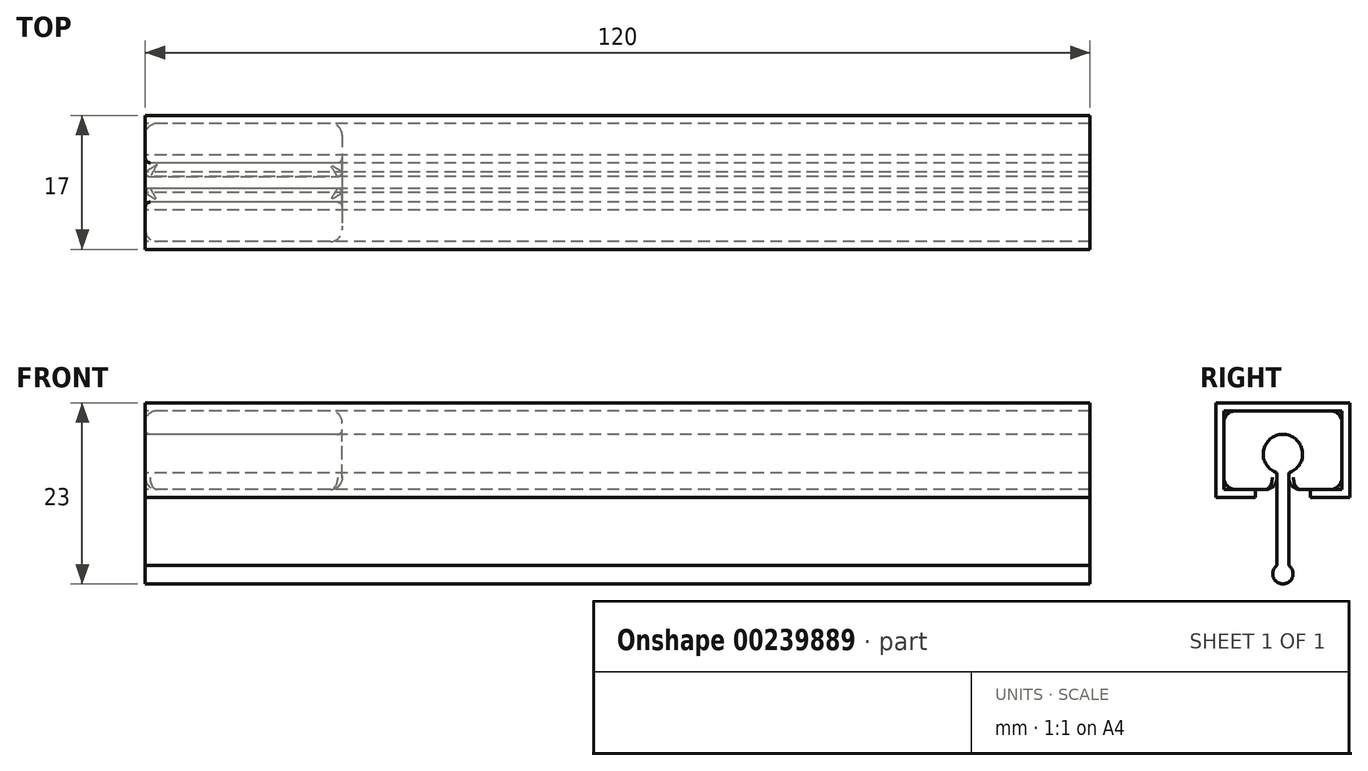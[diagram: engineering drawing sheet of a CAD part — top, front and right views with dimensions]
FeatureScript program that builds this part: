
annotation { "Feature Type Name" : "Feature", "Feature Type Description" : "" }
export const myFeature = defineFeature(function(context is Context, id is Id, definition is map)
    precondition{}
    {
        {
            var Q0;
            Q0=qCreatedBy(makeId("Right.planeOp"),FACE);
            var sketch = newSketch(context, id + "F0", { "sketchPlane" : qUnion([Q0])});
            skArc(sketch, "E0", {"start": v(0.75, -2.88) * mm, "mid": v(0, 2) * mm, "end": v(-0.75, -2.88) * mm});
            skArc(sketch, "E1", {"start": v(-0.75, -14.64) * mm, "mid": v(0, -17) * mm, "end": v(0.75, -14.64) * mm});
            skLineSegment(sketch, "E2", {"start": v(0.75, -2.88) * mm, "end": v(0.75, -14.64) * mm});
            skLineSegment(sketch, "E3", {"start": v(-0.75, -14.64) * mm, "end": v(-0.75, -2.88) * mm});
            skLineSegment(sketch, "E4.bottom", {"start": v(7.5, -5) * mm, "end": v(-7.5, -5) * mm});
            skLineSegment(sketch, "E4.top", {"start": v(7.5, 5) * mm, "end": v(-7.5, 5) * mm});
            skLineSegment(sketch, "E4.left", {"start": v(7.5, -5) * mm, "end": v(7.5, 5) * mm});
            skLineSegment(sketch, "E4.right", {"start": v(-7.5, -5) * mm, "end": v(-7.5, 5) * mm});
            skPoint(sketch, "E4.middle", {"position": v(0, 0) * mm});
            skSolve(sketch);
        }
        {
            var Q0;
            {var subQ5=sQuery(id+"F0.wireOp",EDGE,"E0");Q0=makeQuery(id+"F0.imprint","IMPRINT",FACE,{"disambiguationData":[TD([[makeQuery(id+"F0.imprint","IMPRINT",EDGE,{"derivedFrom":subQ5}),-1.0]])]});}
            extrude(context, id + "F1", {"entities" : qUnion([Q0]), "depth" : 25 * mm});
        }
        {
            var Q0;
            Q0=makeQuery(id+"F1.opExtrude","SWEPT_FACE",FACE,{"disambiguationData":[OSD([sQuery(id+"F0.wireOp",EDGE,"E4.left")])]});
            var Q1;
            Q1=makeQuery(id+"F1.opExtrude","SWEPT_FACE",FACE,{"disambiguationData":[OSD([sQuery(id+"F0.wireOp",EDGE,"E4.top")])]});
            var Q2;
            Q2=makeQuery(id+"F1.opExtrude","SWEPT_FACE",FACE,{"disambiguationData":[OSD([sQuery(id+"F0.wireOp",EDGE,"E4.right")])]});
            var Q3;
            {var subQ0=sQuery(id+"F0.wireOp",EDGE,"E4.bottom");Q3=makeQuery(id+"F1.opExtrude","SWEPT_FACE",FACE,{"disambiguationData":[OSD([subQ0]),TDD([makeQuery(id+"F0.imprint","IMPRINT",EDGE,{"disambiguationData":[TD([[makeQuery(id+"F0.imprint","INTERSECT",VERTEX,{"derivedFrom":[subQ0,sQuery(id+"F0.wireOp",EDGE,"E4.right")]}),1.0]])],"derivedFrom":subQ0})])]});}
            var Q4;
            {var subQ0=sQuery(id+"F0.wireOp",EDGE,"E4.bottom");Q4=makeQuery(id+"F1.opExtrude","SWEPT_FACE",FACE,{"disambiguationData":[OSD([subQ0]),TDD([makeQuery(id+"F0.imprint","IMPRINT",EDGE,{"disambiguationData":[TD([[makeQuery(id+"F0.imprint","INTERSECT",VERTEX,{"derivedFrom":[subQ0,sQuery(id+"F0.wireOp",EDGE,"E4.left")]}),-1.0]])],"derivedFrom":subQ0})])]});}
            var Q5;
            {var subQ0=sQuery(id+"F0.wireOp",EDGE,"E4.bottom");Q5=makeQuery(id+"F1.opExtrude","CAP_EDGE",EDGE,{"disambiguationData":[OSD([subQ0]),TDD([makeQuery(id+"F0.imprint","IMPRINT",EDGE,{"disambiguationData":[TD([[makeQuery(id+"F0.imprint","INTERSECT",VERTEX,{"derivedFrom":[subQ0,sQuery(id+"F0.wireOp",EDGE,"E4.left")]}),-1.0]])],"derivedFrom":subQ0})])],"isStart":false});}
            var Q6;
            Q6=makeQuery(id+"F1.opExtrude","SWEPT_EDGE",EDGE,{"disambiguationData":[OSD([sQuery(id+"F0.wireOp",EDGE,"E4.bottom"),sQuery(id+"F0.wireOp",EDGE,"E4.left")])]});
            var Q7;
            Q7=makeQuery(id+"F1.opExtrude","SWEPT_EDGE",EDGE,{"disambiguationData":[OSD([sQuery(id+"F0.wireOp",EDGE,"E4.bottom"),sQuery(id+"F0.wireOp",EDGE,"E4.right")])]});
            fillet(context, id + "F2", {"entities" : qUnion([Q0, Q1, Q2, Q3, Q4, Q5, Q6, Q7]), "radius" : 1.5 * mm, "tangentPropagation" : true, "allowEdgeOverflow" : false});
        }
        {
            var Q0;
            Q0=makeQuery(id+"F1.opExtrude","SWEPT_FACE",FACE,{"disambiguationData":[OSD([sQuery(id+"F0.wireOp",EDGE,"E0")])]});
            var Q1;
            Q1=makeQuery(id+"F1.opExtrude","CAP_EDGE",EDGE,{"disambiguationData":[OSD([sQuery(id+"F0.wireOp",EDGE,"E3")])],"isStart":false});
            var Q2;
            Q2=makeQuery(id+"F1.opExtrude","CAP_EDGE",EDGE,{"disambiguationData":[OSD([sQuery(id+"F0.wireOp",EDGE,"E2")])],"isStart":false});
            var Q3;
            Q3=makeQuery(id+"F1.opExtrude","CAP_EDGE",EDGE,{"disambiguationData":[OSD([sQuery(id+"F0.wireOp",EDGE,"E3")])],"isStart":true});
            var Q4;
            Q4=makeQuery(id+"F1.opExtrude","CAP_EDGE",EDGE,{"disambiguationData":[OSD([sQuery(id+"F0.wireOp",EDGE,"E2")])],"isStart":true});
            fillet(context, id + "F3", {"entities" : qUnion([Q0, Q1, Q2, Q3, Q4]), "radius" : .6 * mm, "tangentPropagation" : true, "allowEdgeOverflow" : false});
        }
        {
            var Q0;
            {var subQ0=sQuery(id+"F0.wireOp",EDGE,"E0");Q0=makeQuery(id+"F0.imprint","IMPRINT",FACE,{"disambiguationData":[TD([[makeQuery(id+"F0.imprint","IMPRINT",EDGE,{"derivedFrom":subQ0}),1.0]])]});}
            var Q1;
            {var subQ0=sQuery(id+"F0.wireOp",EDGE,"E1");Q1=makeQuery(id+"F0.imprint","IMPRINT",FACE,{"disambiguationData":[TD([[makeQuery(id+"F0.imprint","IMPRINT",EDGE,{"derivedFrom":subQ0}),1.0]])]});}
            extrude(context, id + "F4", {"entities" : qUnion([Q0, Q1]), "depth" : 120 * mm});
        }
        {
            var Q0;
            Q0=qCreatedBy(makeId("Right.planeOp"),FACE);
            var sketch = newSketch(context, id + "F5", { "sketchPlane" : qUnion([Q0])});
            skLineSegment(sketch, "E5.bottom", {"start": v(-7.5, -5) * mm, "end": v(7.5, -5) * mm});
            skLineSegment(sketch, "E5.top", {"start": v(-7.5, 5) * mm, "end": v(7.5, 5) * mm});
            skLineSegment(sketch, "E5.left", {"start": v(-7.5, -5) * mm, "end": v(-7.5, 5) * mm});
            skLineSegment(sketch, "E5.right", {"start": v(7.5, -5) * mm, "end": v(7.5, 5) * mm});
            skPoint(sketch, "E5.middle", {"position": v(0, 0) * mm});
            skLineSegment(sketch, "E6.bottom", {"start": v(-8.5, -6) * mm, "end": v(8.5, -6) * mm});
            skLineSegment(sketch, "E6.top", {"start": v(-8.5, 6) * mm, "end": v(8.5, 6) * mm});
            skLineSegment(sketch, "E6.left", {"start": v(-8.5, -6) * mm, "end": v(-8.5, 6) * mm});
            skLineSegment(sketch, "E6.right", {"start": v(8.5, -6) * mm, "end": v(8.5, 6) * mm});
            skLineSegment(sketch, "E7", {"start": v(3.5, -5) * mm, "end": v(3.5, -6) * mm});
            skLineSegment(sketch, "E8", {"start": v(-3.5, -5) * mm, "end": v(-3.5, -6) * mm});
            skSolve(sketch);
        }
        {
            var Q0;
            Q0=makeQuery(id+"F5.imprint","IMPRINT",FACE,{"disambiguationData":[TD([[makeQuery(id+"F5.imprint","IMPRINT",EDGE,{"derivedFrom":sQuery(id+"F5.wireOp",EDGE,"E5.top")}),1.0]])]});
            extrude(context, id + "F6", {"entities" : qUnion([Q0]), "depth" : 120 * mm});
        }
    });
